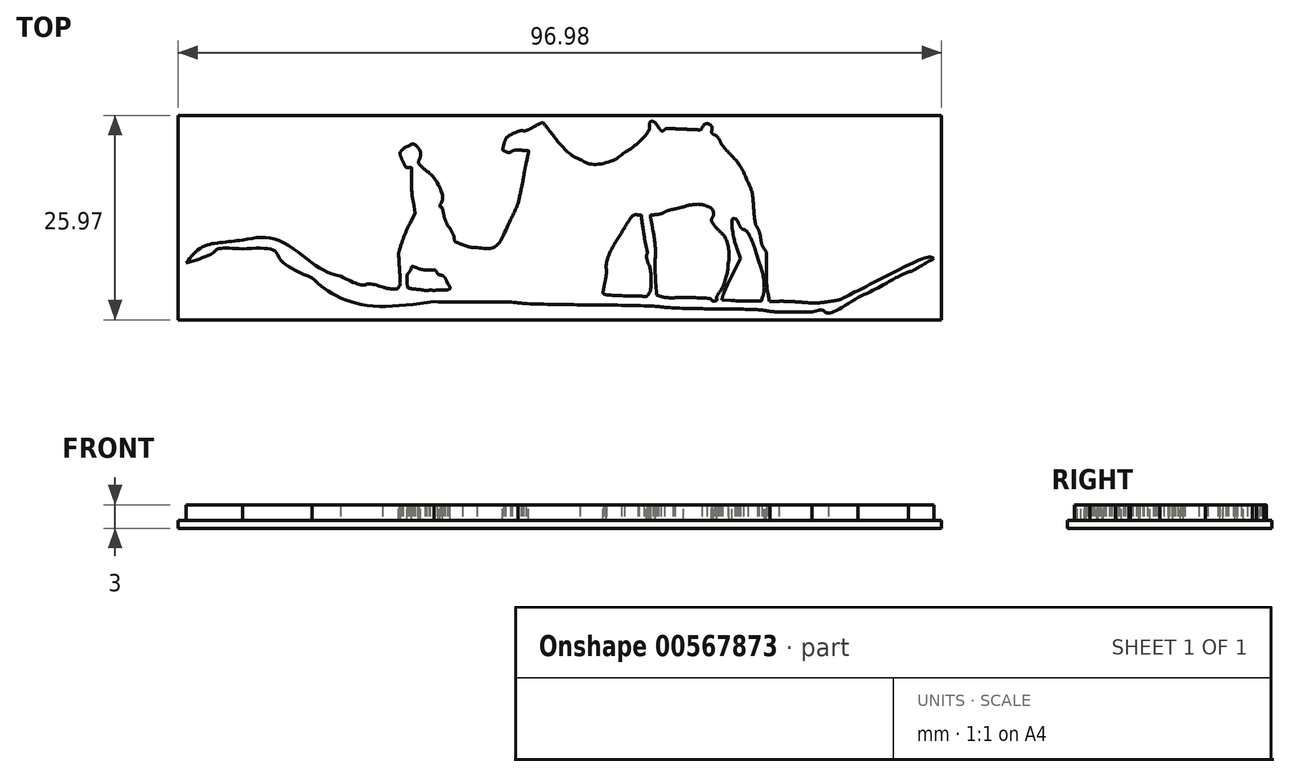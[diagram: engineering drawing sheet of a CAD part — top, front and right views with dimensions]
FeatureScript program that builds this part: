
annotation { "Feature Type Name" : "Feature", "Feature Type Description" : "" }
export const myFeature = defineFeature(function(context is Context, id is Id, definition is map)
    precondition{}
    {
        {
            var Q0;
            Q0=qCreatedBy(makeId("Top.planeOp"),FACE);
            var sketch = newSketch(context, id + "F0", { "sketchPlane" : qUnion([Q0])});
            skPoint(sketch, "E0.middle", {"position": v(0, 0) * mm});
            skFitSpline(sketch, "E1", {"points": [v(26.7, -11.93) * mm, v(25.66, -11.75) * mm, v(23.58, -11.65) * mm, v(20.02, -11.6) * mm]});
            skFitSpline(sketch, "E2", {"points": [v(20.02, -11.6) * mm, v(17.17, -11.57) * mm, v(14.02, -11.46) * mm, v(13, -11.36) * mm]});
            skFitSpline(sketch, "E3", {"points": [v(13, -11.36) * mm, v(12, -11.27) * mm, v(7.87, -11.15) * mm, v(3.83, -11.1) * mm]});
            skFitSpline(sketch, "E4", {"points": [v(3.83, -11.1) * mm, v(-0.2, -11.05) * mm, v(-4.31, -10.93) * mm, v(-5.3, -10.84) * mm]});
            skFitSpline(sketch, "E5", {"points": [v(-5.3, -10.84) * mm, v(-6.28, -10.75) * mm, v(-11.08, -10.75) * mm, v(-15.97, -10.7) * mm]});
            skFitSpline(sketch, "E6", {"points": [v(-15.97, -10.7) * mm, v(-24.16, -11.2) * mm, v(-28.99, -9.62) * mm, v(-31.48, -7.69) * mm]});
            skFitSpline(sketch, "E7", {"points": [v(-31.48, -7.69) * mm, v(-35.44, -5.43) * mm, v(-36.3, -4.22) * mm, v(-40.29, -4) * mm]});
            skFitSpline(sketch, "E8", {"points": [v(-40.29, -4) * mm, v(-43.5, -4.01) * mm, v(-44.02, -4.46) * mm, v(-47.5, -5.8) * mm]});
            skFitSpline(sketch, "E9", {"points": [v(-47.5, -5.8) * mm, v(-45.49, -3.77) * mm, v(-43.1, -3.18) * mm, v(-40.24, -2.86) * mm]});
            skFitSpline(sketch, "E10", {"points": [v(-40.24, -2.86) * mm, v(-35.9, -2.82) * mm, v(-30.7, -6.32) * mm, v(-27.85, -7.45) * mm]});
            skFitSpline(sketch, "E11", {"points": [v(-27.85, -7.45) * mm, v(-25.01, -8.6) * mm, v(-24.29, -8.43) * mm, v(-22.55, -8.84) * mm]});
            skFitSpline(sketch, "E12", {"points": [v(-22.55, -8.84) * mm, v(-22.19, -8.93) * mm, v(-20.69, -9.05) * mm, v(-20.45, -8.77) * mm]});
            skFitSpline(sketch, "E13", {"points": [v(-20.45, -8.77) * mm, v(-20.31, -8.6) * mm, v(-20.29, -7.98) * mm, v(-20.37, -6.51) * mm]});
            skFitSpline(sketch, "E14", {"points": [v(-20.37, -6.51) * mm, v(-20.48, -4.67) * mm, v(-20.46, -4.39) * mm, v(-20.1, -3.3) * mm]});
            skFitSpline(sketch, "E15", {"points": [v(-20.1, -3.3) * mm, v(-19.9, -2.63) * mm, v(-19.42, -1.49) * mm, v(-19.05, -0.76) * mm]});
            skFitSpline(sketch, "E16", {"points": [v(-18.62, 1.91) * mm, v(-18.75, 2.65) * mm, v(-18.85, 3.95) * mm, v(-18.84, 4.8) * mm]});
            skFitSpline(sketch, "E17", {"points": [v(-18.84, 4.8) * mm, v(-18.83, 6.29) * mm, v(-18.84, 6.34) * mm, v(-19.2, 6.34) * mm]});
            skFitSpline(sketch, "E18", {"points": [v(-19.2, 6.34) * mm, v(-19.48, 6.34) * mm, v(-19.66, 6.53) * mm, v(-19.93, 7.09) * mm]});
            skFitSpline(sketch, "E19", {"points": [v(-19.93, 7.09) * mm, v(-20.12, 7.5) * mm, v(-20.28, 7.94) * mm, v(-20.28, 8.06) * mm]});
            skFitSpline(sketch, "E20", {"points": [v(-20.28, 8.06) * mm, v(-20.28, 8.32) * mm, v(-19.66, 8.91) * mm, v(-19.22, 9.07) * mm]});
            skFitSpline(sketch, "E21", {"points": [v(-19.22, 9.07) * mm, v(-18.52, 9.31) * mm, v(-17.71, 8.24) * mm, v(-17.9, 7.3) * mm]});
            skFitSpline(sketch, "E22", {"points": [v(-17.9, 7.3) * mm, v(-17.96, 6.93) * mm, v(-17.84, 6.73) * mm, v(-17.15, 6.1) * mm]});
            skFitSpline(sketch, "E23", {"points": [v(-17.15, 6.1) * mm, v(-15.99, 5.03) * mm, v(-14.9, 2.56) * mm, v(-15.2, 1.65) * mm]});
            skFitSpline(sketch, "E24", {"points": [v(-15.2, 1.65) * mm, v(-15.25, 1.48) * mm, v(-15.22, 1.33) * mm, v(-15.13, 1.33) * mm]});
            skFitSpline(sketch, "E25", {"points": [v(-15.13, 1.33) * mm, v(-15.04, 1.33) * mm, v(-14.87, 0.91) * mm, v(-14.75, 0.4) * mm]});
            skFitSpline(sketch, "E26", {"points": [v(-14.75, 0.4) * mm, v(-14.64, -0.12) * mm, v(-14.32, -0.87) * mm, v(-14.05, -1.28) * mm]});
            skFitSpline(sketch, "E27", {"points": [v(-14.05, -1.28) * mm, v(-13.78, -1.7) * mm, v(-13.5, -2.26) * mm, v(-13.45, -2.54) * mm]});
            skFitSpline(sketch, "E28", {"points": [v(-13.45, -2.54) * mm, v(-13.36, -2.99) * mm, v(-13.2, -3.1) * mm, v(-12.35, -3.44) * mm]});
            skFitSpline(sketch, "E29", {"points": [v(-12.35, -3.44) * mm, v(-11.8, -3.65) * mm, v(-10.97, -3.83) * mm, v(-10.5, -3.83) * mm]});
            skFitSpline(sketch, "E30", {"points": [v(-10.5, -3.83) * mm, v(-8.53, -3.85) * mm, v(-7.65, -3.1) * mm, v(-6.27, -0.25) * mm]});
            skFitSpline(sketch, "E31", {"points": [v(-6.27, -0.25) * mm, v(-5.48, 1.37) * mm, v(-5.21, 2.24) * mm, v(-4.91, 3.65) * mm]});
            skFitSpline(sketch, "E32", {"points": [v(-4.91, 3.65) * mm, v(-4.7, 4.7) * mm, v(-4.46, 6.1) * mm, v(-4.33, 6.7) * mm]});
            skFitSpline(sketch, "E33", {"points": [v(-4.33, 6.7) * mm, v(-3.96, 8.44) * mm, v(-3.97, 8.46) * mm, v(-4.89, 8.55) * mm]});
            skFitSpline(sketch, "E34", {"points": [v(-4.89, 8.55) * mm, v(-5.33, 8.59) * mm, v(-5.86, 8.53) * mm, v(-6.09, 8.42) * mm]});
            skFitSpline(sketch, "E35", {"points": [v(-6.09, 8.42) * mm, v(-6.39, 8.27) * mm, v(-6.6, 8.26) * mm, v(-6.89, 8.4) * mm]});
            skFitSpline(sketch, "E36", {"points": [v(-6.89, 8.4) * mm, v(-7.21, 8.54) * mm, v(-7.26, 8.65) * mm, v(-7.17, 9.08) * mm]});
            skFitSpline(sketch, "E37", {"points": [v(-7.17, 9.08) * mm, v(-7.1, 9.36) * mm, v(-7, 9.7) * mm, v(-6.92, 9.85) * mm]});
            skFitSpline(sketch, "E38", {"points": [v(-6.92, 9.85) * mm, v(-6.76, 10.17) * mm, v(-5.08, 11.01) * mm, v(-4.6, 11.01) * mm]});
            skFitSpline(sketch, "E39", {"points": [v(-4.6, 11.01) * mm, v(-4.42, 11.01) * mm, v(-3.98, 11.16) * mm, v(-3.64, 11.34) * mm]});
            skFitSpline(sketch, "E40", {"points": [v(-3.64, 11.34) * mm, v(-2.3, 12.04) * mm, v(-2.12, 11.98) * mm, v(-1.03, 10.64) * mm]});
            skFitSpline(sketch, "E41", {"points": [v(-1.03, 10.64) * mm, v(0.14, 9.19) * mm, v(1.71, 7.77) * mm, v(2.56, 7.4) * mm]});
            skFitSpline(sketch, "E42", {"points": [v(2.56, 7.4) * mm, v(3.94, 6.79) * mm, v(6.6, 7.2) * mm, v(8.23, 8.27) * mm]});
            skFitSpline(sketch, "E43", {"points": [v(8.23, 8.27) * mm, v(9.44, 9.07) * mm, v(11.26, 10.96) * mm, v(11.37, 11.55) * mm]});
            skFitSpline(sketch, "E44", {"points": [v(11.37, 11.55) * mm, v(11.5, 12.17) * mm, v(11.95, 12.15) * mm, v(12.5, 11.48) * mm]});
            skFitSpline(sketch, "E45", {"points": [v(12.5, 11.48) * mm, v(12.88, 11.04) * mm, v(13, 10.98) * mm, v(13.25, 11.14) * mm]});
            skFitSpline(sketch, "E46", {"points": [v(13.25, 11.14) * mm, v(13.46, 11.26) * mm, v(14.25, 11.3) * mm, v(15.7, 11.23) * mm]});
            skFitSpline(sketch, "E47", {"points": [v(15.7, 11.23) * mm, v(17.57, 11.14) * mm, v(17.88, 11.17) * mm, v(18.08, 11.4) * mm]});
            skFitSpline(sketch, "E48", {"points": [v(18.08, 11.4) * mm, v(18.5, 11.91) * mm, v(19.27, 11.63) * mm, v(19.27, 10.97) * mm]});
            skFitSpline(sketch, "E49", {"points": [v(19.27, 10.97) * mm, v(19.27, 10.8) * mm, v(19.44, 10.59) * mm, v(19.66, 10.5) * mm]});
            skFitSpline(sketch, "E50", {"points": [v(19.66, 10.5) * mm, v(19.88, 10.4) * mm, v(20.18, 10.05) * mm, v(20.33, 9.73) * mm]});
            skFitSpline(sketch, "E51", {"points": [v(20.33, 9.73) * mm, v(20.48, 9.42) * mm, v(20.93, 8.8) * mm, v(21.32, 8.37) * mm]});
            skFitSpline(sketch, "E52", {"points": [v(21.32, 8.37) * mm, v(22.48, 7.11) * mm, v(23.25, 5.94) * mm, v(23.86, 4.53) * mm]});
            skFitSpline(sketch, "E53", {"points": [v(23.86, 4.53) * mm, v(24.34, 3.44) * mm, v(24.46, 2.89) * mm, v(24.6, 1.26) * mm]});
            skFitSpline(sketch, "E54", {"points": [v(24.6, 1.26) * mm, v(24.72, -0.01) * mm, v(24.88, -0.9) * mm, v(25.09, -1.3) * mm]});
            skFitSpline(sketch, "E55", {"points": [v(25.09, -1.3) * mm, v(25.26, -1.64) * mm, v(25.45, -2.26) * mm, v(25.5, -2.68) * mm]});
            skFitSpline(sketch, "E56", {"points": [v(25.5, -2.68) * mm, v(25.57, -3.1) * mm, v(25.76, -3.67) * mm, v(25.94, -3.97) * mm]});
            skFitSpline(sketch, "E57", {"points": [v(25.94, -3.97) * mm, v(26.22, -4.42) * mm, v(26.26, -4.79) * mm, v(26.24, -6.55) * mm]});
            skFitSpline(sketch, "E58", {"points": [v(26.24, -6.55) * mm, v(26.23, -7.67) * mm, v(26.32, -9.05) * mm, v(26.43, -9.61) * mm]});
            skLineSegment(sketch, "E59", {"start": v(-19.05, -0.76) * mm, "end": v(-18.39, 0.58) * mm});
            skLineSegment(sketch, "E60", {"start": v(-18.39, 0.58) * mm, "end": v(-18.62, 1.91) * mm});
            skFitSpline(sketch, "E61", {"points": [v(27.84, -10.64) * mm, v(28.5, -10.64) * mm, v(29.84, -10.7) * mm, v(30.83, -10.77) * mm]});
            skFitSpline(sketch, "E62", {"points": [v(30.83, -10.77) * mm, v(32.1, -10.86) * mm, v(33.06, -10.83) * mm, v(34.08, -10.67) * mm]});
            skFitSpline(sketch, "E63", {"points": [v(34.08, -10.67) * mm, v(35.42, -10.47) * mm, v(35.87, -10.28) * mm, v(39.72, -8.33) * mm]});
            skFitSpline(sketch, "E64", {"points": [v(39.72, -8.33) * mm, v(43.61, -6.35) * mm, v(46.93, -5.02) * mm, v(47.5, -5.21) * mm]});
            skFitSpline(sketch, "E65", {"points": [v(47.5, -5.21) * mm, v(45.59, -6.32) * mm, v(44.86, -6.73) * mm, v(44.3, -6.9) * mm]});
            skFitSpline(sketch, "E66", {"points": [v(44.3, -6.9) * mm, v(42.86, -7.57) * mm, v(41.25, -8.48) * mm, v(37.87, -10.16) * mm]});
            skFitSpline(sketch, "E67", {"points": [v(37.87, -10.16) * mm, v(33.93, -12.13) * mm, v(33.41, -11.77) * mm, v(32.05, -12) * mm]});
            skFitSpline(sketch, "E68", {"points": [v(32.05, -12) * mm, v(30.61, -12) * mm, v(27.7, -12) * mm, v(26.7, -11.93) * mm]});
            skLineSegment(sketch, "E69", {"start": v(26.43, -9.61) * mm, "end": v(26.64, -10.64) * mm});
            skLineSegment(sketch, "E70", {"start": v(26.64, -10.64) * mm, "end": v(27.84, -10.64) * mm});
            skFitSpline(sketch, "E71", {"points": [v(25.68, -10.26) * mm, v(25.94, -9.3) * mm, v(25.76, -7.18) * mm, v(25.29, -5.63) * mm]});
            skFitSpline(sketch, "E72", {"points": [v(25.29, -5.63) * mm, v(24.71, -3.77) * mm, v(23.74, -1.75) * mm, v(23.3, -1.52) * mm]});
            skFitSpline(sketch, "E73", {"points": [v(23.3, -1.52) * mm, v(23.12, -1.42) * mm, v(22.86, -1.08) * mm, v(22.7, -0.76) * mm]});
            skFitSpline(sketch, "E74", {"points": [v(22.7, -0.76) * mm, v(22.55, -0.43) * mm, v(22.35, -0.17) * mm, v(22.26, -0.17) * mm]});
            skFitSpline(sketch, "E75", {"points": [v(22.26, -0.17) * mm, v(21.93, -0.17) * mm, v(22.1, -2.62) * mm, v(22.5, -3.92) * mm]});
            skFitSpline(sketch, "E76", {"points": [v(21.85, -7.4) * mm, v(21.27, -8.6) * mm, v(20.74, -9.8) * mm, v(20.68, -10.05) * mm]});
            skLineSegment(sketch, "E77", {"start": v(22.5, -3.92) * mm, "end": v(22.9, -5.19) * mm});
            skLineSegment(sketch, "E78", {"start": v(22.9, -5.19) * mm, "end": v(21.85, -7.4) * mm});
            skFitSpline(sketch, "E79", {"points": [v(21.71, -10.55) * mm, v(22.34, -10.58) * mm, v(23.47, -10.6) * mm, v(24.22, -10.6) * mm]});
            skFitSpline(sketch, "E80", {"points": [v(24.22, -10.6) * mm, v(25.45, -10.6) * mm, v(25.6, -10.56) * mm, v(25.68, -10.26) * mm]});
            skLineSegment(sketch, "E81", {"start": v(20.68, -10.05) * mm, "end": v(20.57, -10.5) * mm});
            skLineSegment(sketch, "E82", {"start": v(20.57, -10.5) * mm, "end": v(21.71, -10.55) * mm});
            skFitSpline(sketch, "E83", {"points": [v(19.9, -10.3) * mm, v(19.88, -10.19) * mm, v(20, -9.9) * mm, v(20.16, -9.65) * mm]});
            skFitSpline(sketch, "E84", {"points": [v(20.16, -9.65) * mm, v(20.62, -8.95) * mm, v(21.26, -6.98) * mm, v(21.37, -5.9) * mm]});
            skFitSpline(sketch, "E85", {"points": [v(21.37, -5.9) * mm, v(21.5, -4.65) * mm, v(20.97, -2.5) * mm, v(20.4, -1.86) * mm]});
            skFitSpline(sketch, "E86", {"points": [v(20.4, -1.86) * mm, v(19.68, -1.09) * mm, v(19.23, -0.33) * mm, v(19.33, -0.08) * mm]});
            skFitSpline(sketch, "E87", {"points": [v(19.33, -0.08) * mm, v(19.54, 0.47) * mm, v(19.23, 1.2) * mm, v(18.7, 1.41) * mm]});
            skFitSpline(sketch, "E88", {"points": [v(18.7, 1.41) * mm, v(18.12, 1.64) * mm, v(16.69, 1.62) * mm, v(15.68, 1.35) * mm]});
            skFitSpline(sketch, "E89", {"points": [v(15.68, 1.35) * mm, v(15.31, 1.26) * mm, v(14.71, 1.12) * mm, v(14.34, 1.04) * mm]});
            skFitSpline(sketch, "E90", {"points": [v(14.34, 1.04) * mm, v(13.98, 0.96) * mm, v(13.5, 0.8) * mm, v(13.26, 0.67) * mm]});
            skFitSpline(sketch, "E91", {"points": [v(13.26, 0.67) * mm, v(13.04, 0.55) * mm, v(12.55, 0.41) * mm, v(12.18, 0.37) * mm]});
            skFitSpline(sketch, "E92", {"points": [v(12.18, 0.37) * mm, v(11.81, 0.33) * mm, v(11.5, 0.29) * mm, v(11.5, 0.27) * mm]});
            skFitSpline(sketch, "E93", {"points": [v(11.5, 0.27) * mm, v(11.48, 0.26) * mm, v(11.63, -0.58) * mm, v(11.8, -1.59) * mm]});
            skFitSpline(sketch, "E94", {"points": [v(11.8, -1.59) * mm, v(12.01, -2.77) * mm, v(12.12, -4.08) * mm, v(12.1, -5.26) * mm]});
            skFitSpline(sketch, "E95", {"points": [v(12.1, -5.26) * mm, v(12.1, -6.27) * mm, v(12.13, -7.7) * mm, v(12.19, -8.46) * mm]});
            skFitSpline(sketch, "E96", {"points": [v(12.85, -10.01) * mm, v(13.15, -10.11) * mm, v(13.95, -10.2) * mm, v(14.62, -10.2) * mm]});
            skFitSpline(sketch, "E97", {"points": [v(14.62, -10.2) * mm, v(16.29, -10.18) * mm, v(19.14, -10.33) * mm, v(19.24, -10.43) * mm]});
            skFitSpline(sketch, "E98", {"points": [v(19.24, -10.43) * mm, v(19.41, -10.6) * mm, v(19.95, -10.5) * mm, v(19.9, -10.3) * mm]});
            skLineSegment(sketch, "E99", {"start": v(12.19, -8.46) * mm, "end": v(12.29, -9.83) * mm});
            skLineSegment(sketch, "E100", {"start": v(12.29, -9.83) * mm, "end": v(12.85, -10.01) * mm});
            skFitSpline(sketch, "E101", {"points": [v(11.25, -9.69) * mm, v(11.5, -9.21) * mm, v(11.47, -6.48) * mm, v(11.2, -5.82) * mm]});
            skFitSpline(sketch, "E102", {"points": [v(11.2, -5.82) * mm, v(10.98, -4.84) * mm, v(11.02, -4.75) * mm, v(11.04, -4.68) * mm]});
            skFitSpline(sketch, "E103", {"points": [v(11.04, -4.68) * mm, v(11.12, -4.4) * mm, v(11.11, -4.4) * mm, v(11.08, -4.23) * mm]});
            skFitSpline(sketch, "E104", {"points": [v(11.08, -4.23) * mm, v(11.05, -4.06) * mm, v(10.83, -3.1) * mm, v(10.68, -2.09) * mm]});
            skFitSpline(sketch, "E105", {"points": [v(10.68, -2.09) * mm, v(10.34, 0.21) * mm, v(10.3, 0.33) * mm, v(9.93, 0.33) * mm]});
            skFitSpline(sketch, "E106", {"points": [v(9.93, 0.33) * mm, v(9.4, 0.33) * mm, v(8.85, -0.26) * mm, v(7.8, -1.95) * mm]});
            skFitSpline(sketch, "E107", {"points": [v(7.8, -1.95) * mm, v(6.75, -3.64) * mm, v(5.92, -5.73) * mm, v(5.91, -6.7) * mm]});
            skFitSpline(sketch, "E108", {"points": [v(5.91, -6.7) * mm, v(5.9, -7) * mm, v(5.8, -7.78) * mm, v(5.68, -8.43) * mm]});
            skFitSpline(sketch, "E109", {"points": [v(5.68, -8.43) * mm, v(5.55, -9.07) * mm, v(5.48, -9.63) * mm, v(5.52, -9.67) * mm]});
            skFitSpline(sketch, "E110", {"points": [v(5.52, -9.67) * mm, v(5.6, -9.75) * mm, v(8.38, -9.94) * mm, v(10.04, -9.99) * mm]});
            skFitSpline(sketch, "E111", {"points": [v(10.04, -9.99) * mm, v(10.91, -10) * mm, v(11.1, -9.96) * mm, v(11.25, -9.69) * mm]});
            skFitSpline(sketch, "E112", {"points": [v(0.74, -9.57) * mm, v(1.15, -9.6) * mm, v(1.58, -9.58) * mm, v(2.7, -9.62) * mm]});
            skFitSpline(sketch, "E113", {"points": [v(4.84, -9.06) * mm, v(4.9, -8.71) * mm, v(5.05, -7.9) * mm, v(5.19, -7.27) * mm]});
            skFitSpline(sketch, "E114", {"points": [v(5.19, -7.27) * mm, v(5.34, -6.54) * mm, v(5.4, -5.8) * mm, v(5.33, -5.24) * mm]});
            skFitSpline(sketch, "E115", {"points": [v(5.33, -5.24) * mm, v(5.2, -4.3) * mm, v(5.18, -4.36) * mm, v(6.4, -2.17) * mm]});
            skFitSpline(sketch, "E116", {"points": [v(6.4, -2.17) * mm, v(6.8, -1.48) * mm, v(7.26, -0.47) * mm, v(7.44, 0.07) * mm]});
            skFitSpline(sketch, "E117", {"points": [v(7.44, 0.07) * mm, v(7.76, 1.02) * mm, v(7.77, 1.09) * mm, v(7.5, 1.8) * mm]});
            skFitSpline(sketch, "E118", {"points": [v(7.5, 1.8) * mm, v(7.16, 2.67) * mm, v(6.43, 3.5) * mm, v(6, 3.5) * mm]});
            skFitSpline(sketch, "E119", {"points": [v(6, 3.5) * mm, v(5.33, 3.5) * mm, v(2.98, 4.07) * mm, v(2.18, 4.42) * mm]});
            skFitSpline(sketch, "E120", {"points": [v(2.18, 4.42) * mm, v(1.33, 4.8) * mm, v(0.1, 5.72) * mm, v(-1.5, 7.2) * mm]});
            skFitSpline(sketch, "E121", {"points": [v(-1.5, 7.2) * mm, v(-1.97, 7.63) * mm, v(-2.65, 8.16) * mm, v(-3.05, 8.23) * mm]});
            skFitSpline(sketch, "E122", {"points": [v(-3.05, 8.23) * mm, v(-3.31, 8.27) * mm, v(-3.27, 8.2) * mm, v(-3.57, 6.6) * mm]});
            skFitSpline(sketch, "E123", {"points": [v(-3.57, 6.6) * mm, v(-4.3, 2.7) * mm, v(-4.8, 1.08) * mm, v(-5.7, -0.73) * mm]});
            skFitSpline(sketch, "E124", {"points": [v(-5.7, -0.73) * mm, v(-6.25, -1.87) * mm, v(-7.06, -3.25) * mm, v(-7.5, -3.57) * mm]});
            skFitSpline(sketch, "E125", {"points": [v(-7.5, -3.57) * mm, v(-8.01, -4.03) * mm, v(-8.87, -4.46) * mm, v(-9.48, -4.54) * mm]});
            skFitSpline(sketch, "E126", {"points": [v(-9.48, -4.54) * mm, v(-10.05, -4.71) * mm, v(-11.8, -4.36) * mm, v(-12.09, -4.31) * mm]});
            skFitSpline(sketch, "E127", {"points": [v(-12.09, -4.31) * mm, v(-12.85, -4.14) * mm, v(-12.68, -4.7) * mm, v(-12.47, -4.95) * mm]});
            skFitSpline(sketch, "E128", {"points": [v(-12.47, -4.95) * mm, v(-12.02, -5.07) * mm, v(-11.7, -5.65) * mm, v(-11.94, -5.93) * mm]});
            skFitSpline(sketch, "E129", {"points": [v(-11.94, -5.93) * mm, v(-12.08, -6.1) * mm, v(-12.08, -6.25) * mm, v(-11.93, -6.51) * mm]});
            skFitSpline(sketch, "E130", {"points": [v(-11.93, -6.51) * mm, v(-11.52, -7.3) * mm, v(-12.2, -7.6) * mm, v(-13.12, -7.06) * mm]});
            skFitSpline(sketch, "E131", {"points": [v(-13.12, -7.06) * mm, v(-13.58, -6.79) * mm, v(-13.62, -6.79) * mm, v(-13.89, -7.05) * mm]});
            skFitSpline(sketch, "E132", {"points": [v(-13.89, -7.05) * mm, v(-13.97, -7.24) * mm, v(-13.95, -7.4) * mm, v(-13.9, -7.53) * mm]});
            skFitSpline(sketch, "E133", {"points": [v(-13.9, -7.53) * mm, v(-13.75, -7.86) * mm, v(-13.47, -8.1) * mm, v(-13.2, -8.45) * mm]});
            skFitSpline(sketch, "E134", {"points": [v(-13.2, -8.45) * mm, v(-12.86, -8.97) * mm, v(-12.6, -9.17) * mm, v(-12.16, -9.25) * mm]});
            skFitSpline(sketch, "E135", {"points": [v(-12.16, -9.25) * mm, v(-11.84, -9.32) * mm, v(-9.1, -9.4) * mm, v(-6.05, -9.44) * mm]});
            skFitSpline(sketch, "E136", {"points": [v(-6.05, -9.44) * mm, v(-3.02, -9.48) * mm, v(-0.7, -9.52) * mm, v(-0.46, -9.55) * mm]});
            skFitSpline(sketch, "E137", {"points": [v(-0.46, -9.55) * mm, v(-0.08, -9.58) * mm, v(0.25, -9.55) * mm, v(0.74, -9.57) * mm]});
            skLineSegment(sketch, "E138", {"start": v(2.7, -9.62) * mm, "end": v(4.73, -9.7) * mm});
            skLineSegment(sketch, "E139", {"start": v(4.73, -9.7) * mm, "end": v(4.84, -9.06) * mm});
            skFitSpline(sketch, "E140", {"points": [v(-15.47, -9.21) * mm, v(-14.13, -9.14) * mm, v(-13.96, -8.97) * mm, v(-14.3, -8.34) * mm]});
            skFitSpline(sketch, "E141", {"points": [v(-14.3, -8.34) * mm, v(-14.35, -8.21) * mm, v(-14.43, -7.99) * mm, v(-14.61, -7.64) * mm]});
            skFitSpline(sketch, "E142", {"points": [v(-14.61, -7.64) * mm, v(-14.75, -7.46) * mm, v(-14.83, -7.4) * mm, v(-15.02, -7.34) * mm]});
            skFitSpline(sketch, "E143", {"points": [v(-15.02, -7.34) * mm, v(-15.25, -7.27) * mm, v(-15.5, -7.2) * mm, v(-15.6, -7) * mm]});
            skFitSpline(sketch, "E144", {"points": [v(-15.6, -7) * mm, v(-15.75, -6.75) * mm, v(-15.96, -6.68) * mm, v(-16.6, -6.68) * mm]});
            skFitSpline(sketch, "E145", {"points": [v(-16.6, -6.68) * mm, v(-17.04, -6.68) * mm, v(-17.71, -6.56) * mm, v(-18.1, -6.43) * mm]});
            skFitSpline(sketch, "E146", {"points": [v(-18.1, -6.43) * mm, v(-18.73, -6.2) * mm, v(-18.8, -6.2) * mm, v(-18.9, -6.47) * mm]});
            skFitSpline(sketch, "E147", {"points": [v(-18.9, -6.47) * mm, v(-18.95, -6.63) * mm, v(-19.1, -6.88) * mm, v(-19.23, -7.03) * mm]});
            skFitSpline(sketch, "E148", {"points": [v(-19.23, -7.03) * mm, v(-19.38, -7.2) * mm, v(-19.44, -7.6) * mm, v(-19.41, -8.1) * mm]});
            skFitSpline(sketch, "E149", {"points": [v(-19.41, -8.1) * mm, v(-19.37, -8.83) * mm, v(-19.31, -8.92) * mm, v(-18.89, -9.03) * mm]});
            skFitSpline(sketch, "E150", {"points": [v(-18.89, -9.03) * mm, v(-18.62, -9.1) * mm, v(-18.32, -9.1) * mm, v(-18.12, -9.12) * mm]});
            skFitSpline(sketch, "E151", {"points": [v(-18.12, -9.12) * mm, v(-17.67, -9.16) * mm, v(-17.26, -9.24) * mm, v(-16.94, -9.26) * mm]});
            skFitSpline(sketch, "E152", {"points": [v(-16.94, -9.26) * mm, v(-16.76, -9.26) * mm, v(-16.68, -9.24) * mm, v(-16.5, -9.24) * mm]});
            skFitSpline(sketch, "E153", {"points": [v(-16.5, -9.24) * mm, v(-16.32, -9.22) * mm, v(-16.14, -9.25) * mm, v(-15.47, -9.21) * mm]});
            skLineSegment(sketch, "E154", {"start": v(-15.47, -9.21) * mm, "end": v(-15.47, -9.21) * mm});
            skSolve(sketch);
        }
        {
            var Q0;
            Q0=makeQuery(id+"F0.imprint","IMPRINT",FACE,{"disambiguationData":[TD([[makeQuery(id+"F0.imprint","IMPRINT",EDGE,{"derivedFrom":sQuery(id+"F0.wireOp",EDGE,"E1")}),-1.0]])]});
            extrude(context, id + "F1", {"entities" : qUnion([Q0]), "depth" : 2 * mm, "offsetDistance" : 25 * mm});
        }
        {
            var Q0;
            Q0=makeQuery(id+"F1.opExtrude","CAP_FACE",FACE,{"disambiguationData":[OSD([sQuery(id+"F0.wireOp",EDGE,"E1"),sQuery(id+"F0.wireOp",EDGE,"E2"),sQuery(id+"F0.wireOp",EDGE,"E3"),sQuery(id+"F0.wireOp",EDGE,"E4"),sQuery(id+"F0.wireOp",EDGE,"E5"),sQuery(id+"F0.wireOp",EDGE,"E6"),sQuery(id+"F0.wireOp",EDGE,"E7"),sQuery(id+"F0.wireOp",EDGE,"E8"),sQuery(id+"F0.wireOp",EDGE,"E9"),sQuery(id+"F0.wireOp",EDGE,"E10"),sQuery(id+"F0.wireOp",EDGE,"E11"),sQuery(id+"F0.wireOp",EDGE,"E12"),sQuery(id+"F0.wireOp",EDGE,"E13"),sQuery(id+"F0.wireOp",EDGE,"E14"),sQuery(id+"F0.wireOp",EDGE,"E15"),sQuery(id+"F0.wireOp",EDGE,"E16"),sQuery(id+"F0.wireOp",EDGE,"E17"),sQuery(id+"F0.wireOp",EDGE,"E18"),sQuery(id+"F0.wireOp",EDGE,"E19"),sQuery(id+"F0.wireOp",EDGE,"E20"),sQuery(id+"F0.wireOp",EDGE,"E21"),sQuery(id+"F0.wireOp",EDGE,"E22"),sQuery(id+"F0.wireOp",EDGE,"E23"),sQuery(id+"F0.wireOp",EDGE,"E24"),sQuery(id+"F0.wireOp",EDGE,"E25"),sQuery(id+"F0.wireOp",EDGE,"E26"),sQuery(id+"F0.wireOp",EDGE,"E27"),sQuery(id+"F0.wireOp",EDGE,"E28"),sQuery(id+"F0.wireOp",EDGE,"E29"),sQuery(id+"F0.wireOp",EDGE,"E30"),sQuery(id+"F0.wireOp",EDGE,"E31"),sQuery(id+"F0.wireOp",EDGE,"E32"),sQuery(id+"F0.wireOp",EDGE,"E33"),sQuery(id+"F0.wireOp",EDGE,"E34"),sQuery(id+"F0.wireOp",EDGE,"E35"),sQuery(id+"F0.wireOp",EDGE,"E36"),sQuery(id+"F0.wireOp",EDGE,"E37"),sQuery(id+"F0.wireOp",EDGE,"E38"),sQuery(id+"F0.wireOp",EDGE,"E39"),sQuery(id+"F0.wireOp",EDGE,"E40"),sQuery(id+"F0.wireOp",EDGE,"E41"),sQuery(id+"F0.wireOp",EDGE,"E42"),sQuery(id+"F0.wireOp",EDGE,"E43"),sQuery(id+"F0.wireOp",EDGE,"E44"),sQuery(id+"F0.wireOp",EDGE,"E45"),sQuery(id+"F0.wireOp",EDGE,"E46"),sQuery(id+"F0.wireOp",EDGE,"E47"),sQuery(id+"F0.wireOp",EDGE,"E48"),sQuery(id+"F0.wireOp",EDGE,"E49"),sQuery(id+"F0.wireOp",EDGE,"E50"),sQuery(id+"F0.wireOp",EDGE,"E51"),sQuery(id+"F0.wireOp",EDGE,"E52"),sQuery(id+"F0.wireOp",EDGE,"E53"),sQuery(id+"F0.wireOp",EDGE,"E54"),sQuery(id+"F0.wireOp",EDGE,"E55"),sQuery(id+"F0.wireOp",EDGE,"E56"),sQuery(id+"F0.wireOp",EDGE,"E57"),sQuery(id+"F0.wireOp",EDGE,"E58"),sQuery(id+"F0.wireOp",EDGE,"E59"),sQuery(id+"F0.wireOp",EDGE,"E60"),sQuery(id+"F0.wireOp",EDGE,"E61"),sQuery(id+"F0.wireOp",EDGE,"E62"),sQuery(id+"F0.wireOp",EDGE,"E63"),sQuery(id+"F0.wireOp",EDGE,"E64"),sQuery(id+"F0.wireOp",EDGE,"E65"),sQuery(id+"F0.wireOp",EDGE,"E66"),sQuery(id+"F0.wireOp",EDGE,"E67"),sQuery(id+"F0.wireOp",EDGE,"E68"),sQuery(id+"F0.wireOp",EDGE,"E69"),sQuery(id+"F0.wireOp",EDGE,"E70"),sQuery(id+"F0.wireOp",EDGE,"E71"),sQuery(id+"F0.wireOp",EDGE,"E72"),sQuery(id+"F0.wireOp",EDGE,"E73"),sQuery(id+"F0.wireOp",EDGE,"E74"),sQuery(id+"F0.wireOp",EDGE,"E75"),sQuery(id+"F0.wireOp",EDGE,"E76"),sQuery(id+"F0.wireOp",EDGE,"E77"),sQuery(id+"F0.wireOp",EDGE,"E78"),sQuery(id+"F0.wireOp",EDGE,"E79"),sQuery(id+"F0.wireOp",EDGE,"E80"),sQuery(id+"F0.wireOp",EDGE,"E81"),sQuery(id+"F0.wireOp",EDGE,"E82"),sQuery(id+"F0.wireOp",EDGE,"E83"),sQuery(id+"F0.wireOp",EDGE,"E84"),sQuery(id+"F0.wireOp",EDGE,"E85"),sQuery(id+"F0.wireOp",EDGE,"E86"),sQuery(id+"F0.wireOp",EDGE,"E87"),sQuery(id+"F0.wireOp",EDGE,"E88"),sQuery(id+"F0.wireOp",EDGE,"E89"),sQuery(id+"F0.wireOp",EDGE,"E90"),sQuery(id+"F0.wireOp",EDGE,"E91"),sQuery(id+"F0.wireOp",EDGE,"E92"),sQuery(id+"F0.wireOp",EDGE,"E93"),sQuery(id+"F0.wireOp",EDGE,"E94"),sQuery(id+"F0.wireOp",EDGE,"E95"),sQuery(id+"F0.wireOp",EDGE,"E96"),sQuery(id+"F0.wireOp",EDGE,"E97"),sQuery(id+"F0.wireOp",EDGE,"E98"),sQuery(id+"F0.wireOp",EDGE,"E99"),sQuery(id+"F0.wireOp",EDGE,"E100"),sQuery(id+"F0.wireOp",EDGE,"E101"),sQuery(id+"F0.wireOp",EDGE,"E102"),sQuery(id+"F0.wireOp",EDGE,"E103"),sQuery(id+"F0.wireOp",EDGE,"E104"),sQuery(id+"F0.wireOp",EDGE,"E105"),sQuery(id+"F0.wireOp",EDGE,"E106"),sQuery(id+"F0.wireOp",EDGE,"E107"),sQuery(id+"F0.wireOp",EDGE,"E108"),sQuery(id+"F0.wireOp",EDGE,"E109"),sQuery(id+"F0.wireOp",EDGE,"E110"),sQuery(id+"F0.wireOp",EDGE,"E111"),sQuery(id+"F0.wireOp",EDGE,"E112"),sQuery(id+"F0.wireOp",EDGE,"E113"),sQuery(id+"F0.wireOp",EDGE,"E114"),sQuery(id+"F0.wireOp",EDGE,"E115"),sQuery(id+"F0.wireOp",EDGE,"E116"),sQuery(id+"F0.wireOp",EDGE,"E117"),sQuery(id+"F0.wireOp",EDGE,"E118"),sQuery(id+"F0.wireOp",EDGE,"E119"),sQuery(id+"F0.wireOp",EDGE,"E120"),sQuery(id+"F0.wireOp",EDGE,"E121"),sQuery(id+"F0.wireOp",EDGE,"E122"),sQuery(id+"F0.wireOp",EDGE,"E123"),sQuery(id+"F0.wireOp",EDGE,"E124"),sQuery(id+"F0.wireOp",EDGE,"E125"),sQuery(id+"F0.wireOp",EDGE,"E126"),sQuery(id+"F0.wireOp",EDGE,"E127"),sQuery(id+"F0.wireOp",EDGE,"E128"),sQuery(id+"F0.wireOp",EDGE,"E129"),sQuery(id+"F0.wireOp",EDGE,"E130"),sQuery(id+"F0.wireOp",EDGE,"E131"),sQuery(id+"F0.wireOp",EDGE,"E132"),sQuery(id+"F0.wireOp",EDGE,"E133"),sQuery(id+"F0.wireOp",EDGE,"E134"),sQuery(id+"F0.wireOp",EDGE,"E135"),sQuery(id+"F0.wireOp",EDGE,"E136"),sQuery(id+"F0.wireOp",EDGE,"E137"),sQuery(id+"F0.wireOp",EDGE,"E138"),sQuery(id+"F0.wireOp",EDGE,"E139"),sQuery(id+"F0.wireOp",EDGE,"E140"),sQuery(id+"F0.wireOp",EDGE,"E141"),sQuery(id+"F0.wireOp",EDGE,"E142"),sQuery(id+"F0.wireOp",EDGE,"E143"),sQuery(id+"F0.wireOp",EDGE,"E144"),sQuery(id+"F0.wireOp",EDGE,"E145"),sQuery(id+"F0.wireOp",EDGE,"E146"),sQuery(id+"F0.wireOp",EDGE,"E147"),sQuery(id+"F0.wireOp",EDGE,"E148"),sQuery(id+"F0.wireOp",EDGE,"E149"),sQuery(id+"F0.wireOp",EDGE,"E150"),sQuery(id+"F0.wireOp",EDGE,"E151"),sQuery(id+"F0.wireOp",EDGE,"E152"),sQuery(id+"F0.wireOp",EDGE,"E153")])],"isStart":true});
            var sketch = newSketch(context, id + "F2", { "sketchPlane" : qUnion([Q0])});
            skLineSegment(sketch, "E155.bottom", {"start": v(48.5, 13) * mm, "end": v(-48.5, 13) * mm});
            skLineSegment(sketch, "E155.top", {"start": v(48.5, -12.97) * mm, "end": v(-48.5, -12.97) * mm});
            skLineSegment(sketch, "E155.left", {"start": v(48.5, 13) * mm, "end": v(48.5, -12.97) * mm});
            skLineSegment(sketch, "E155.right", {"start": v(-48.5, 13) * mm, "end": v(-48.5, -12.97) * mm});
            skSolve(sketch);
        }
        {
            var Q0;
            Q0 = qSketchRegion(id + "F2", true);
            extrude(context, id + "F3", {"entities" : qUnion([Q0]), "operationType" : NewBodyOperationType.ADD, "depth" : 1 * mm, "offsetDistance" : 25 * mm});
        }
    });
